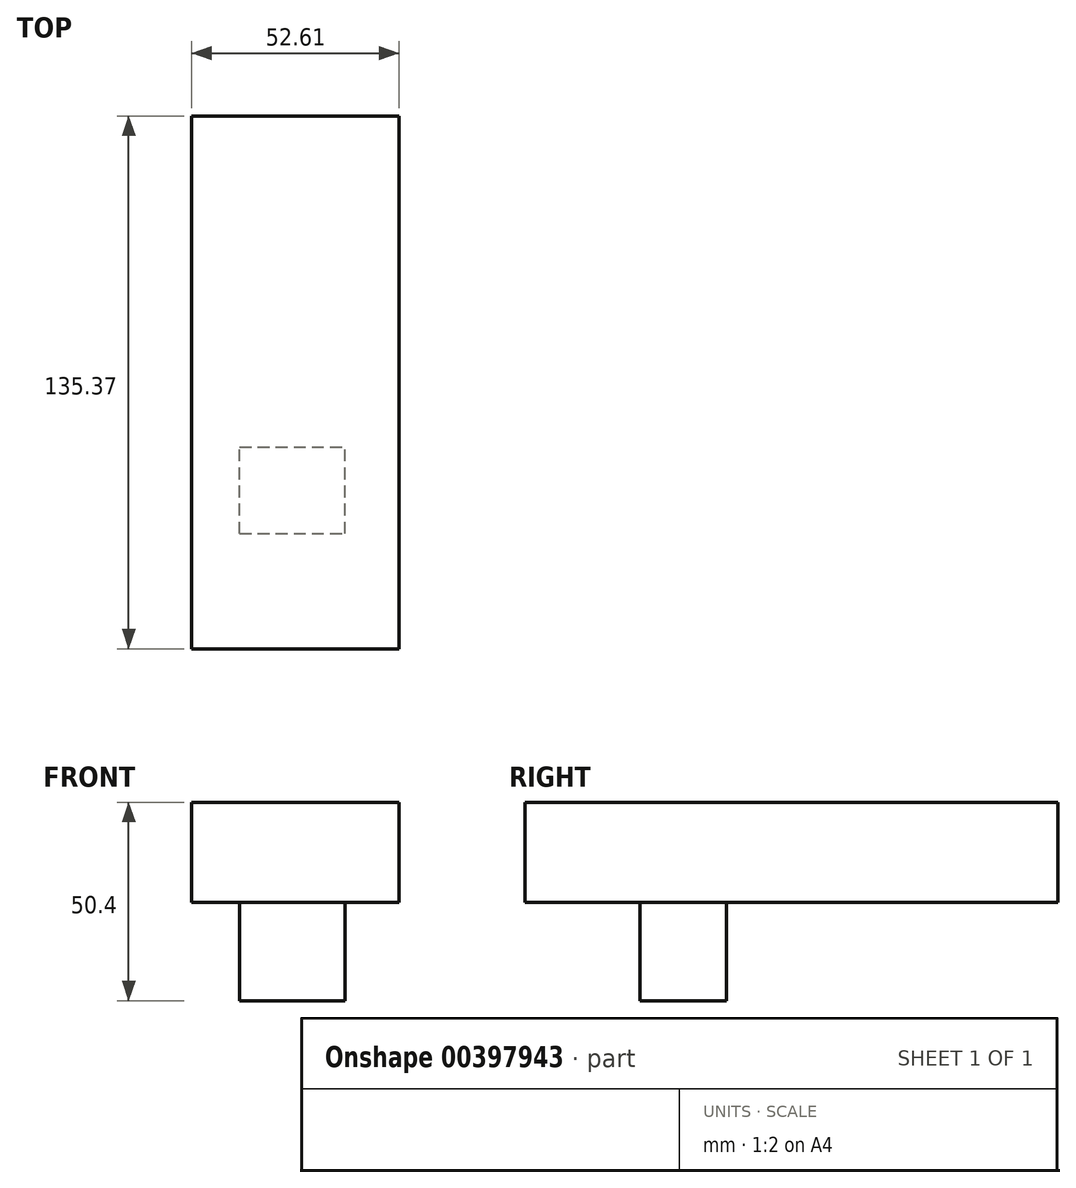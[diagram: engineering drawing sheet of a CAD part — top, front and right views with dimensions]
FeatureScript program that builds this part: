
annotation { "Feature Type Name" : "Feature", "Feature Type Description" : "" }
export const myFeature = defineFeature(function(context is Context, id is Id, definition is map)
    precondition{}
    {
        {
            var Q0;
            Q0=qCreatedBy(makeId("Top.planeOp"),FACE);
            var sketch = newSketch(context, id + "F0", { "sketchPlane" : qUnion([Q0])});
            skLineSegment(sketch, "E0.bottom", {"start": v(-12.13, 70.69) * mm, "end": v(40.48, 70.69) * mm});
            skLineSegment(sketch, "E0.top", {"start": v(-12.13, -64.68) * mm, "end": v(40.48, -64.68) * mm});
            skLineSegment(sketch, "E0.left", {"start": v(-12.13, 70.69) * mm, "end": v(-12.13, -64.68) * mm});
            skLineSegment(sketch, "E0.right", {"start": v(40.48, 70.69) * mm, "end": v(40.48, -64.68) * mm});
            skSolve(sketch);
        }
        {
            var Q0;
            Q0=makeQuery(id+"F0.imprint","IMPRINT",FACE,{"disambiguationData":[TD([[makeQuery(id+"F0.imprint","IMPRINT",EDGE,{"derivedFrom":sQuery(id+"F0.wireOp",EDGE,"E0.bottom")}),-1.0]])]});
            extrude(context, id + "F1", {"entities" : qUnion([Q0]), "depth" : 25.4 * mm});
        }
        {
            var Q0;
            Q0=qCreatedBy(makeId("Top.planeOp"),FACE);
            var sketch = newSketch(context, id + "F2", { "sketchPlane" : qUnion([Q0])});
            skLineSegment(sketch, "E1.bottom", {"start": v(0, -35.4) * mm, "end": v(26.86, -35.4) * mm});
            skLineSegment(sketch, "E1.top", {"start": v(0, -13.44) * mm, "end": v(26.86, -13.44) * mm});
            skLineSegment(sketch, "E1.left", {"start": v(0, -35.4) * mm, "end": v(0, -13.44) * mm});
            skLineSegment(sketch, "E1.right", {"start": v(26.86, -35.4) * mm, "end": v(26.86, -13.44) * mm});
            skSolve(sketch);
        }
        {
            var Q0;
            Q0=makeQuery(id+"F2.imprint","IMPRINT",FACE,{"disambiguationData":[TD([[makeQuery(id+"F2.imprint","IMPRINT",EDGE,{"derivedFrom":sQuery(id+"F2.wireOp",EDGE,"E1.bottom")}),1.0]])]});
            extrude(context, id + "F3", {"entities" : qUnion([Q0]), "operationType" : NewBodyOperationType.ADD, "oppositeDirection" : true, "depth" : 25 * mm});
        }
    });
